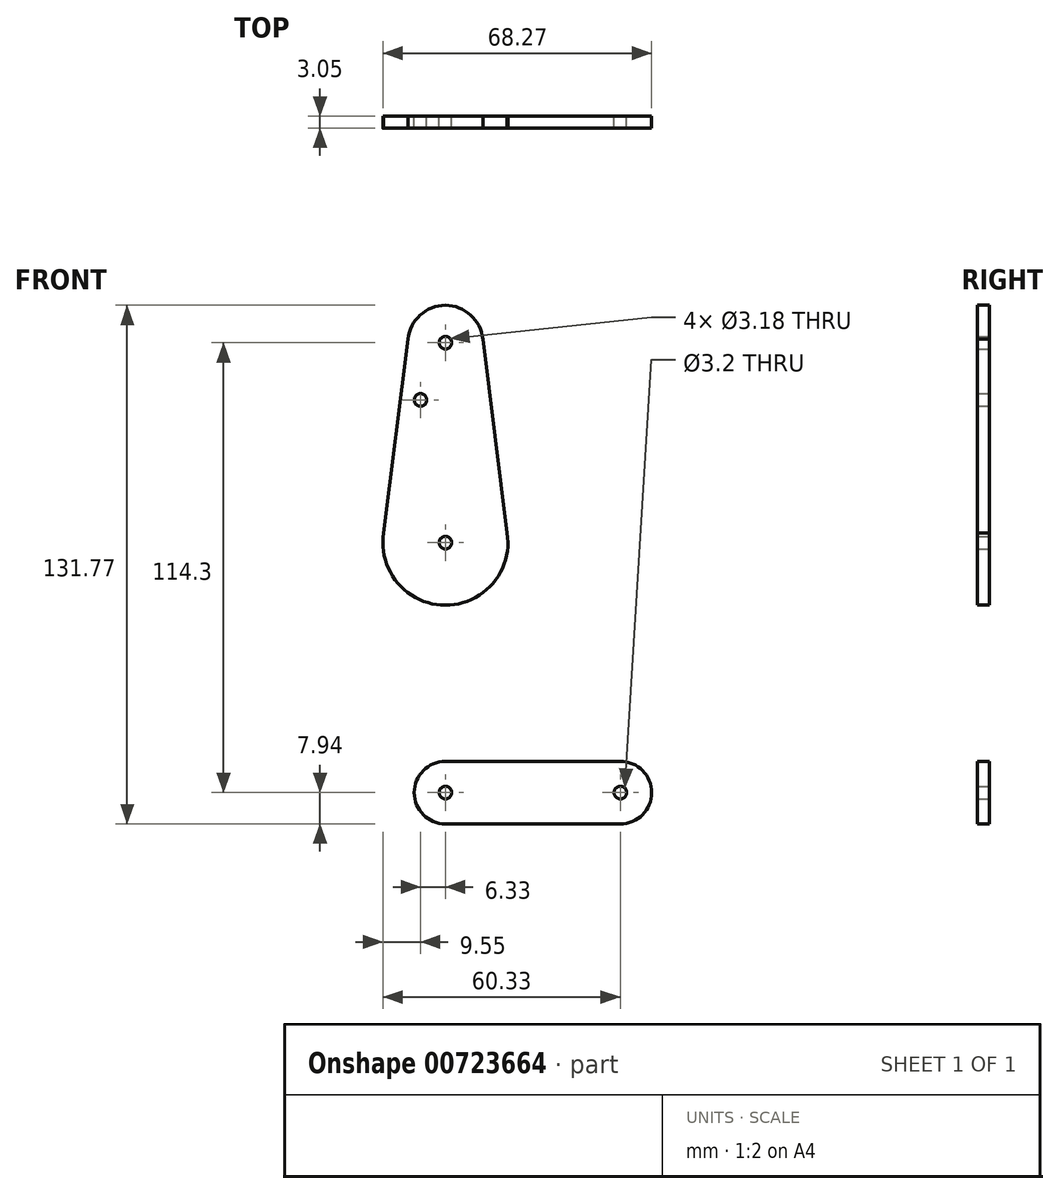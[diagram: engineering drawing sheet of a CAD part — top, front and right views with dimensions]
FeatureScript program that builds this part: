
annotation { "Feature Type Name" : "Feature", "Feature Type Description" : "" }
export const myFeature = defineFeature(function(context is Context, id is Id, definition is map)
    precondition{}
    {
        {
            var Q0;
            Q0=qCreatedBy(makeId("Front.planeOp"),FACE);
            var sketch = newSketch(context, id + "F0", { "sketchPlane" : qUnion([Q0])});
            skLineSegment(sketch, "E0", {"start": v(0, 0) * mm, "end": v(0, 114.3) * mm, "construction": true});
            skLineSegment(sketch, "E1", {"start": v(0, 0) * mm, "end": v(44.45, 0) * mm, "construction": true});
            skCircle(sketch, "E2", {"center": v(0, 114.3) * mm, "radius": 9.53 * mm});
            skCircle(sketch, "E3", {"center": v(0, 63.5) * mm, "radius": 15.88 * mm});
            skCircle(sketch, "E4", {"center": v(0, 0) * mm, "radius": 7.94 * mm});
            skCircle(sketch, "E5", {"center": v(44.45, 0) * mm, "radius": 7.94 * mm});
            skLineSegment(sketch, "E6", {"start": v(9.45, 115.5) * mm, "end": v(15.75, 65.48) * mm});
            skLineSegment(sketch, "E7", {"start": v(-9.45, 115.5) * mm, "end": v(-15.75, 65.48) * mm});
            skLineSegment(sketch, "E8", {"start": v(0, 7.94) * mm, "end": v(44.45, 7.94) * mm});
            skLineSegment(sketch, "E9", {"start": v(0, -7.94) * mm, "end": v(44.45, -7.94) * mm});
            skCircle(sketch, "E10", {"center": v(0, 63.5) * mm, "radius": 1.59 * mm});
            skCircle(sketch, "E11", {"center": v(0, 114.3) * mm, "radius": 1.59 * mm});
            skCircle(sketch, "E12", {"center": v(44.45, 0) * mm, "radius": 1.6 * mm});
            skCircle(sketch, "E13", {"center": v(0, 0) * mm, "radius": 1.59 * mm});
            skCircle(sketch, "E14", {"center": v(-6.33, 99.78) * mm, "radius": 1.59 * mm});
            skLineSegment(sketch, "E15", {"start": v(-15.75, 61.52) * mm, "end": v(-7.88, -1) * mm});
            skLineSegment(sketch, "E16", {"start": v(15.75, 61.52) * mm, "end": v(7.88, -1) * mm});
            skSolve(sketch);
        }
        {
            var Q0;
            Q0 = qSketchRegion(id + "F0", true);
            extrude(context, id + "F1", {"entities" : qUnion([Q0]), "depth" : 3.05 * mm, "offsetDistance" : 25.4 * mm});
        }
        {
            var Q0;
            Q0=makeQuery(id+"F1.opExtrude","SWEPT_BODY",BODY,{"disambiguationData":[OSD([sQuery(id+"F0.wireOp",EDGE,"E4"),sQuery(id+"F0.wireOp",EDGE,"E5"),sQuery(id+"F0.wireOp",EDGE,"E8"),sQuery(id+"F0.wireOp",EDGE,"E9"),sQuery(id+"F0.wireOp",EDGE,"E12"),sQuery(id+"F0.wireOp",EDGE,"E13")])]});
            deleteBodies(context, id + "F2", {"entities" : qUnion([Q0])});
        }
        {
            var Q0;
            Q0=makeQuery(id+"F1.opExtrude","SWEPT_BODY",BODY,{"disambiguationData":[OSD([sQuery(id+"F0.wireOp",EDGE,"E2"),sQuery(id+"F0.wireOp",EDGE,"E3"),sQuery(id+"F0.wireOp",EDGE,"E6"),sQuery(id+"F0.wireOp",EDGE,"E7"),sQuery(id+"F0.wireOp",EDGE,"E10"),sQuery(id+"F0.wireOp",EDGE,"E11"),sQuery(id+"F0.wireOp",EDGE,"E14")])]});
            deleteBodies(context, id + "F3", {"entities" : qUnion([Q0])});
        }
        {
            var Q0;
            Q0 = qSketchRegion(id + "F0", true);
            extrude(context, id + "F4", {"entities" : qUnion([Q0]), "depth" : 3.05 * mm, "offsetDistance" : 25.4 * mm});
        }
    });
